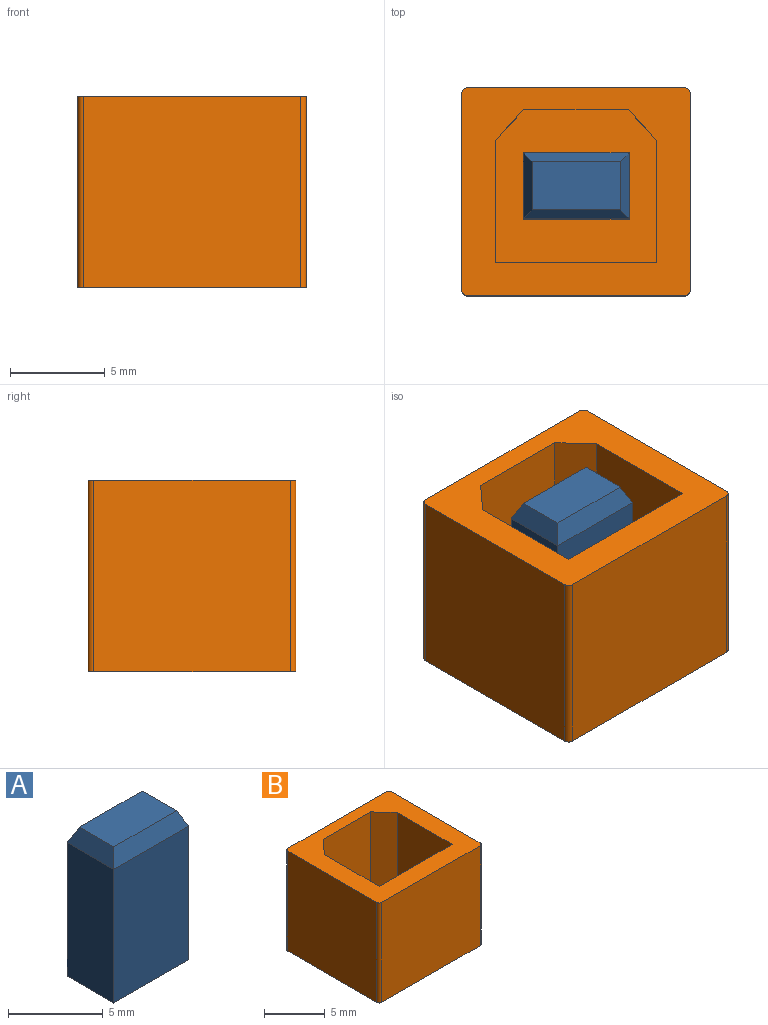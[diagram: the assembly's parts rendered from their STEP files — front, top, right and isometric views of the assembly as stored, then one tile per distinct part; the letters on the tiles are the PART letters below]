
ASSEMBLY  parts=2 mates=1
PART A: 10 faces, bbox 5.6x3.5x9.6 mm
  f0: plane 8.61x5.59mm, normal (0,-1,0), area 48.1mm2, adj f1,f3,f5,f6
  f1: plane 8.61x3.48mm, normal (1,0,0), area 30mm2, adj f0,f6,f7,f9
  f2: plane 3.48x1mm, normal (-0.91,0,0.42), area 3.3mm2, adj f3,f4,f5,f8
  f3: plane 5.59x1mm, normal (0,-0.91,0.42), area 5.7mm2, adj f0,f2,f8,f9
  f4: plane 5.59x1mm, normal (0,0.91,0.42), area 5.7mm2, adj f2,f7,f8,f9
  f5: plane 8.61x3.48mm, normal (-1,0,0), area 30mm2, adj f0,f2,f6,f7
  f6: plane 5.59x3.48mm, normal (0,0,-1), area 19.4mm2, adj f0,f1,f5,f7
  f7: plane 8.61x5.59mm, normal (0,1,0), area 48.1mm2, adj f1,f4,f5,f6
  f8: plane 4.66x2.55mm, normal (0,0,1), area 11.9mm2, adj f2,f3,f4,f9
  f9: plane 3.48x1mm, normal (0.91,0,0.42), area 3.3mm2, adj f1,f3,f4,f8
PART B: 22 faces, bbox 12.1x11x10.1 mm
  f0: plane 9.11x6.43mm, normal (1,0,0), area 58.5mm2, adj f9,f11,f14,f16
  f1: cylinder r=0.3mm len=10.11mm, axis (0,0,1), area 4.8mm2, adj f2,f3,f14,f15
  f2: plane 10.37x10.11mm, normal (-1,0,0), area 104.9mm2, adj f1,f3,f4,f14
  f3: plane 12.07x10.97mm, normal (0,0,-1), area 132.3mm2, adj f1,f2,f4,f5,f6,f12,f13,f15
  f4: cylinder r=0.3mm len=10.11mm, axis (0,0,1), area 4.8mm2, adj f2,f3,f13,f14
  f5: cylinder r=0.3mm len=10.11mm, axis (0,0,1), area 4.8mm2, adj f3,f12,f13,f14
  f6: cylinder r=0.3mm len=10.11mm, axis (0,0,-1), area 4.8mm2, adj f3,f12,f14,f15
  f7: plane 9.11x6.43mm, normal (-1,0,0), area 58.5mm2, adj f8,f11,f14,f16
  f8: plane 9.11x1.63mm, normal (-0.74,-0.67,0), area 20.1mm2, adj f7,f10,f14,f16
  f9: plane 9.11x1.63mm, normal (0.74,-0.67,0), area 20.1mm2, adj f0,f10,f14,f16
  f10: plane 9.11x5.54mm, normal (0,-1,0), area 50.4mm2, adj f8,f9,f14,f16
  f11: plane 9.11x8.51mm, normal (0,1,0), area 77.5mm2, adj f0,f7,f14,f16
  f12: plane 10.37x10.11mm, normal (1,0,0), area 104.9mm2, adj f3,f5,f6,f14
  f13: plane 11.47x10.11mm, normal (0,-1,0), area 115.9mm2, adj f3,f4,f5,f14
  f14: plane 12.07x10.97mm, normal (0,0,1), area 66.2mm2, adj f0,f1,f2,f4,f5,f6,f7,f8
  f15: plane 11.47x10.11mm, normal (0,1,0), area 115.9mm2, adj f1,f3,f6,f14
  f16: plane 8.51x8.05mm, normal (0,0,1), area 46.7mm2, adj f0,f7,f8,f9,f10,f11,f17,f18
  f17: plane 3.48x0.5mm, normal (1,0,0), area 1.7mm2, adj f16,f19,f20,f21
  f18: plane 3.48x0.5mm, normal (-1,0,0), area 1.7mm2, adj f16,f19,f20,f21
  f19: plane 5.59x0.5mm, normal (0,-1,0), area 2.8mm2, adj f16,f17,f18,f20
  f20: plane 5.59x3.48mm, normal (0,0,1), area 19.4mm2, adj f17,f18,f19,f21
  f21: plane 5.59x0.5mm, normal (0,1,0), area 2.8mm2, adj f16,f17,f18,f20
PLACE A at identity
PLACE B at identity
MATE fastened A.f6 <-> B.f20  axis (0,0,-1) through (0,0,-0.5)mm
